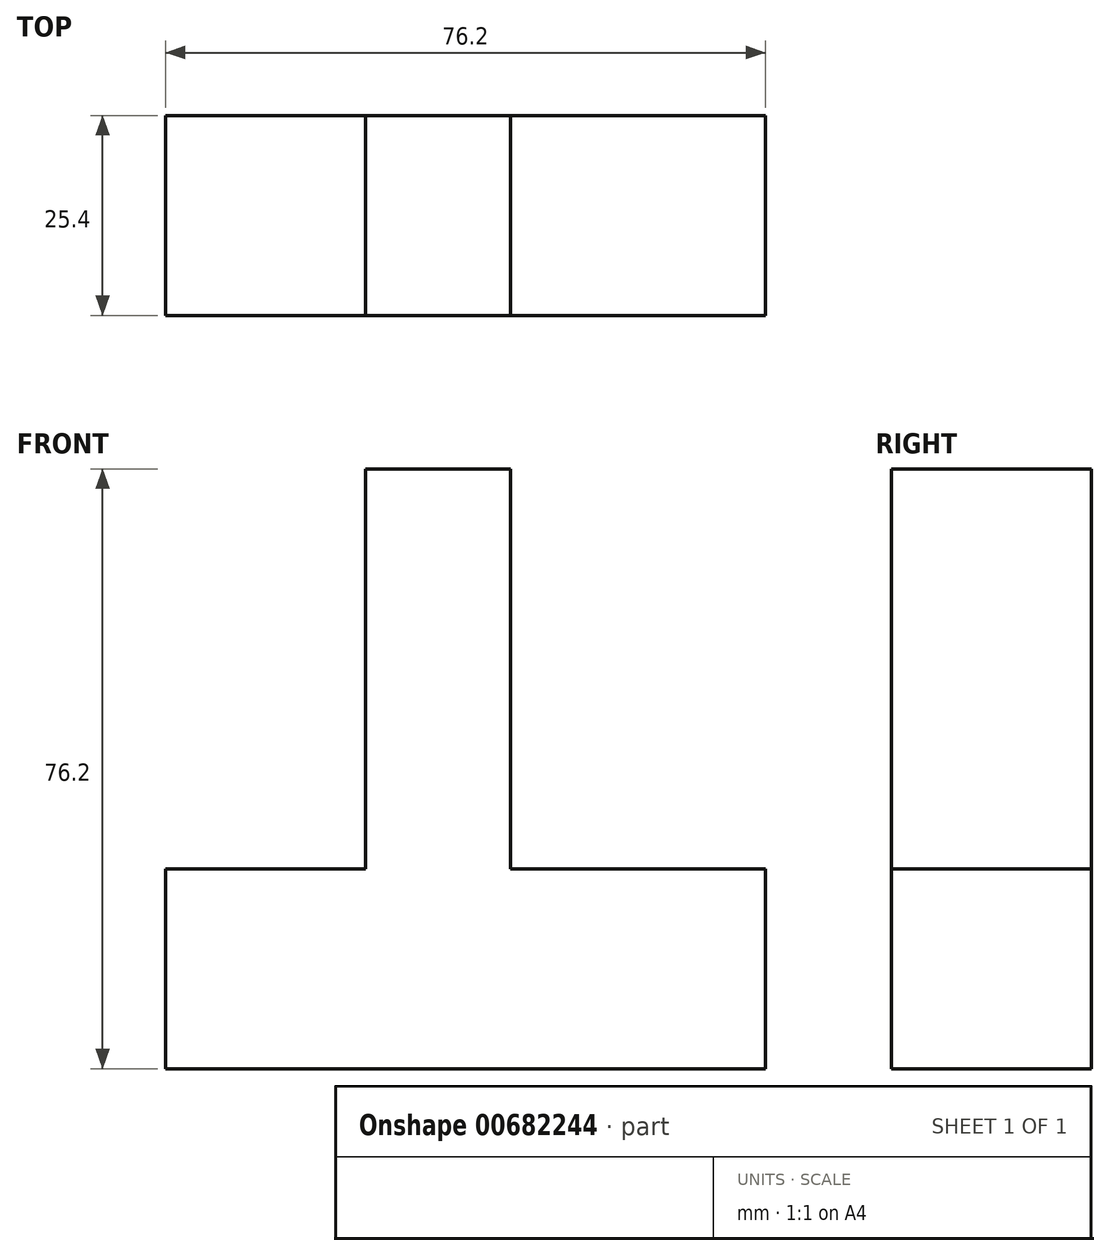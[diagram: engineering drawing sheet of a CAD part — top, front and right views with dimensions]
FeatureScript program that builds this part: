
annotation { "Feature Type Name" : "Feature", "Feature Type Description" : "" }
export const myFeature = defineFeature(function(context is Context, id is Id, definition is map)
    precondition{}
    {
        {
            var Q0;
            Q0=qCreatedBy(makeId("Front.planeOp"),FACE);
            var sketch = newSketch(context, id + "F0", { "sketchPlane" : qUnion([Q0])});
            skLineSegment(sketch, "E0", {"start": v(0, 0) * mm, "end": v(-76.2, 0) * mm});
            skLineSegment(sketch, "E1", {"start": v(-76.2, 0) * mm, "end": v(-76.2, 25.4) * mm});
            skLineSegment(sketch, "E2", {"start": v(-76.2, 25.4) * mm, "end": v(-50.8, 25.4) * mm});
            skLineSegment(sketch, "E3", {"start": v(-50.8, 25.4) * mm, "end": v(-50.8, 76.2) * mm});
            skLineSegment(sketch, "E4", {"start": v(-50.8, 76.2) * mm, "end": v(-32.38, 76.2) * mm});
            skLineSegment(sketch, "E5", {"start": v(-32.38, 76.2) * mm, "end": v(-32.38, 25.4) * mm});
            skPoint(sketch, "E6.start.orphan", {"position": v(-30.08, 25.4) * mm});
            skLineSegment(sketch, "E7", {"start": v(-32.38, 25.4) * mm, "end": v(0, 25.4) * mm});
            skLineSegment(sketch, "E8", {"start": v(0, 25.4) * mm, "end": v(0, 0) * mm});
            skSolve(sketch);
        }
        {
            var Q0;
            Q0 = qSketchRegion(id + "F0", true);
            extrude(context, id + "F1", {"entities" : qUnion([Q0]), "depth" : 25.4 * mm, "offsetDistance" : 25.4 * mm});
        }
    });
